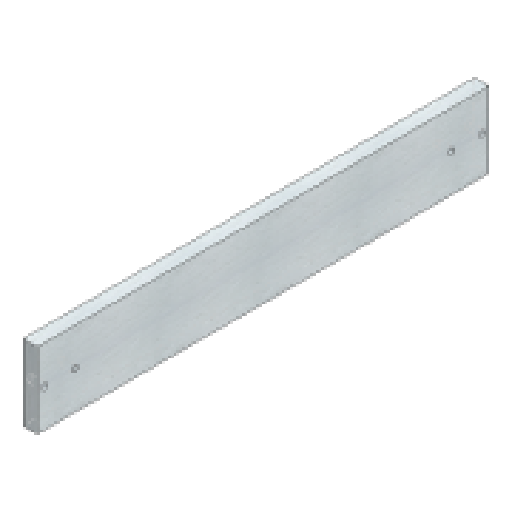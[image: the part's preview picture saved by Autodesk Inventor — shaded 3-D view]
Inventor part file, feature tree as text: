
AUTODESK INVENTOR PART (.ipt)
format: ipt  version: 2024 (Build 280153000, 153)  size: 167,936 bytes
history: native  units: in
note: dims shown in document units (in); Inventor stores cm internally (conversion verified against a paired STEP export)
features: extrude x1, sketch x1
ambient origin geometry x8: Origin, YZ Plane, XZ Plane, XY Plane, X Axis, Y Axis, Z Axis, Center Point
bodies: Solid1 (feature_tree)
feature tree (2):
  extrude  "Extrusion1"  Depth=23.622in
  sketch  "Sketch1"  dims[d0=3.937in d1=23.622in d2=0.374in d3=0.374in d4=0.315in d5=0.315in d6=0.748in d7=0.0in d8=1.9685in d9=0.315in d10=1.9685in d11=0.315in]
